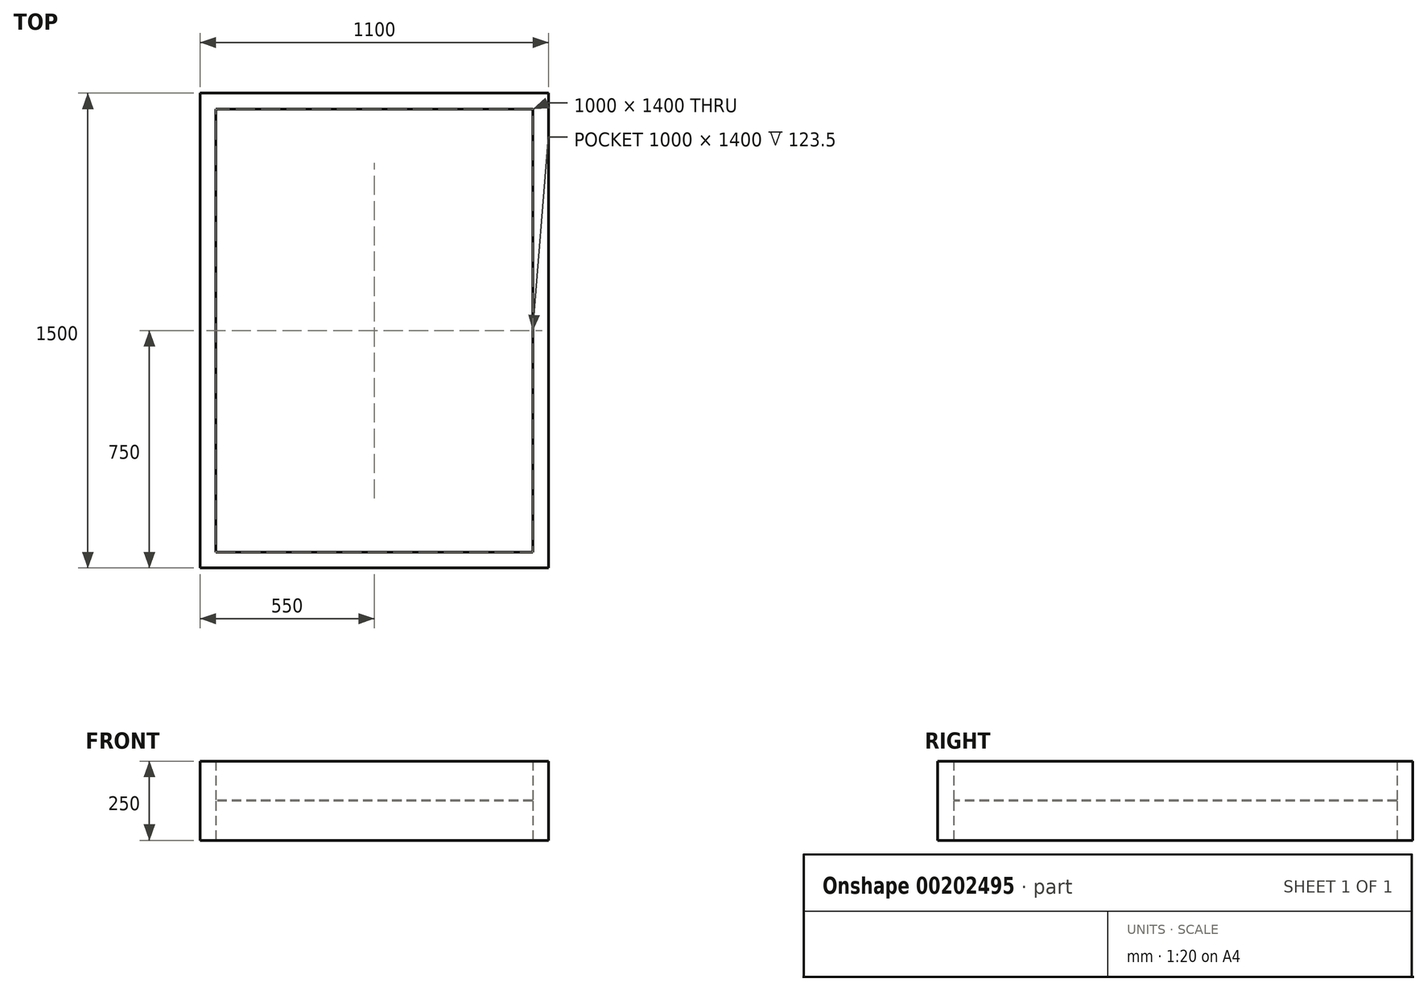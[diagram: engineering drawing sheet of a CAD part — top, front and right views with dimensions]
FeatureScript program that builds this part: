
annotation { "Feature Type Name" : "Feature", "Feature Type Description" : "" }
export const myFeature = defineFeature(function(context is Context, id is Id, definition is map)
    precondition{}
    {
        {
            var Q0;
            Q0=qCreatedBy(makeId("Top.planeOp"),FACE);
            var sketch = newSketch(context, id + "F0", { "sketchPlane" : qUnion([Q0])});
            skLineSegment(sketch, "E0.bottom", {"start": v(550, 750) * mm, "end": v(-550, 750) * mm});
            skLineSegment(sketch, "E0.top", {"start": v(550, -750) * mm, "end": v(-550, -750) * mm});
            skLineSegment(sketch, "E0.left", {"start": v(550, 750) * mm, "end": v(550, -750) * mm});
            skLineSegment(sketch, "E0.right", {"start": v(-550, 750) * mm, "end": v(-550, -750) * mm});
            skPoint(sketch, "E0.middle", {"position": v(0, 0) * mm});
            skLineSegment(sketch, "E1.bottom", {"start": v(500, 700) * mm, "end": v(-500, 700) * mm});
            skLineSegment(sketch, "E1.top", {"start": v(500, -700) * mm, "end": v(-500, -700) * mm});
            skLineSegment(sketch, "E1.left", {"start": v(500, 700) * mm, "end": v(500, -700) * mm});
            skLineSegment(sketch, "E1.right", {"start": v(-500, 700) * mm, "end": v(-500, -700) * mm});
            skSolve(sketch);
        }
        {
            var Q0;
            Q0=makeQuery(id+"F0.imprint","IMPRINT",FACE,{"disambiguationData":[TD([[makeQuery(id+"F0.imprint","IMPRINT",EDGE,{"derivedFrom":sQuery(id+"F0.wireOp",EDGE,"E0.bottom")}),1.0]])]});
            extrude(context, id + "F1", {"entities" : qUnion([Q0]), "endBound" : BoundingType.SYMMETRIC, "depth" : 250 * mm});
        }
        {
            var Q0;
            Q0=qCreatedBy(makeId("Top.planeOp"),FACE);
            var sketch = newSketch(context, id + "F2", { "sketchPlane" : qUnion([Q0])});
            skLineSegment(sketch, "E2.bottom", {"start": v(500, 700) * mm, "end": v(-500, 700) * mm});
            skLineSegment(sketch, "E2.top", {"start": v(500, -700) * mm, "end": v(-500, -700) * mm});
            skLineSegment(sketch, "E2.left", {"start": v(500, 700) * mm, "end": v(500, -700) * mm});
            skLineSegment(sketch, "E2.right", {"start": v(-500, 700) * mm, "end": v(-500, -700) * mm});
            skPoint(sketch, "E2.middle", {"position": v(0, 0) * mm});
            skSolve(sketch);
        }
        {
            var Q0;
            Q0=qSketchRegion(id+"F2",true);
            extrude(context, id + "F3", {"entities" : qUnion([Q0]), "operationType" : NewBodyOperationType.ADD, "endBound" : BoundingType.SYMMETRIC, "depth" : 3 * mm});
        }
    });
